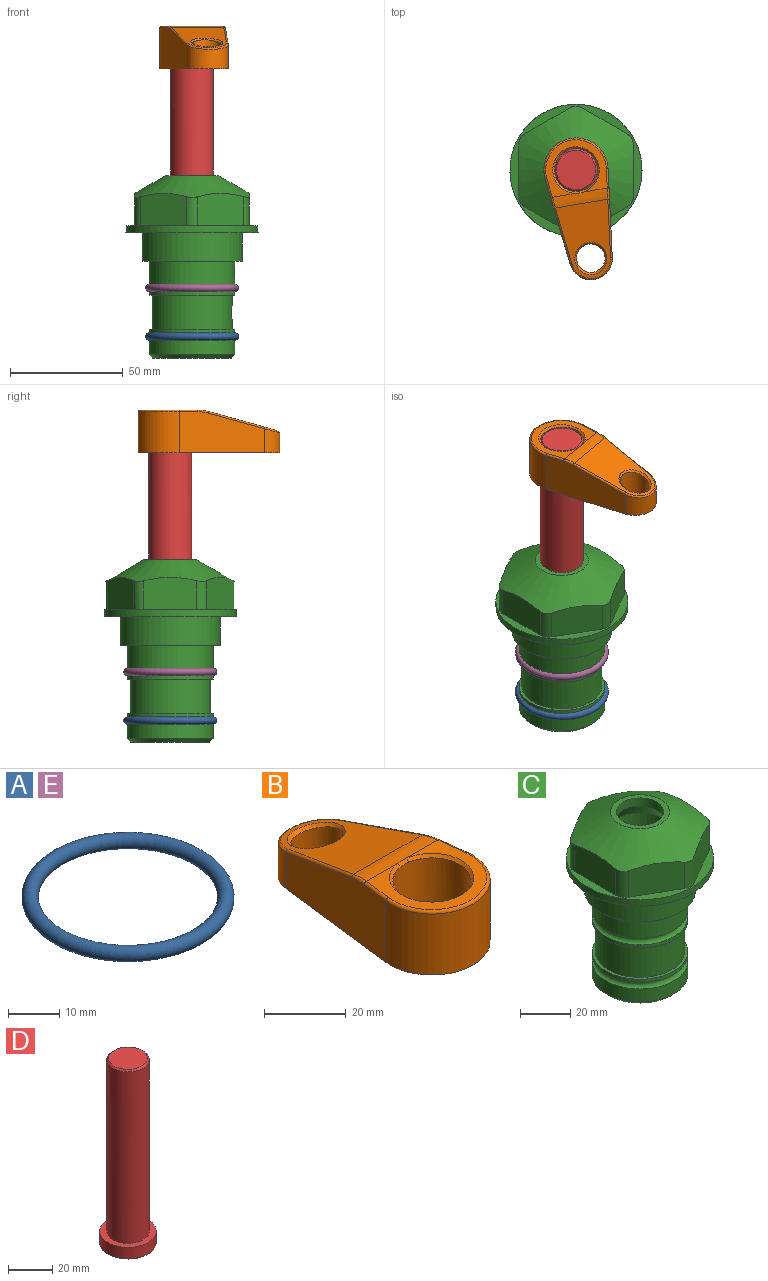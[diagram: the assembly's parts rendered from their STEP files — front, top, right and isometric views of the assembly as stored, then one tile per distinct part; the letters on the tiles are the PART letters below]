
ASSEMBLY  parts=5 mates=4
PART A: 1 faces, bbox 44.7x44.7x3.2 mm
  f0: torus R=19.05mm, axis (0,0,1), area 1193.9mm2
PART B: 31 faces, bbox 31.7x65.5x19.8 mm
  f0: plane 39.12x18.26mm, normal (0.99,0.12,0), area 612.2mm2, adj f1,f4,f7,f11,f13,f15
  f1: cylinder r=9.53mm len=18.91mm, axis (0,0,-1), area 296.1mm2, adj f0,f2,f7,f17
  f2: plane 39.12x18.26mm, normal (-0.99,0.12,0), area 612.2mm2, adj f1,f4,f7,f12,f14,f16
  f3: cylinder r=6.35mm len=12.7mm, axis (0,0,-1), area 362.4mm2, adj f7,f18
  f4: cylinder r=14.29mm len=28.58mm, axis (0,0,-1), area 882.2mm2, adj f0,f2,f7,f10
  f5: cylinder r=9.53mm len=19.05mm, axis (0,0,-1), area 1092.6mm2, adj f7,f19,f20
  f6: plane 26.99x23.69mm, normal (0,0,1), area 216.2mm2, adj f9,f10,f11,f12,f19
  f7: plane 63.5x28.58mm, normal (0,0,-1), area 661.8mm2, adj f0,f1,f2,f3,f4,f5,f22,f23
  f8: plane 33.52x23.6mm, normal (0,0.26,0.97), area 486mm2, adj f9,f15,f16,f17,f18
  f9: cylinder r=19.05mm len=24.72mm, axis (1,0,0), area 120.4mm2, adj f6,f8,f13,f14,f20
  f10: torus R=13.49mm, axis (0,0,1), area 59mm2, adj f4,f6,f11,f12
  f11: cylinder r=0.79mm len=8.67mm, axis (0.12,-0.99,0), area 10.8mm2, adj f0,f6,f10,f13
  f12: cylinder r=0.79mm len=8.67mm, axis (0.12,0.99,0), area 10.8mm2, adj f2,f6,f10,f14
  f13: bspline ~4.95x1.42mm, area 6.1mm2, adj f0,f9,f11,f15
  f14: bspline ~4.95x1.42mm, area 6.1mm2, adj f2,f9,f12,f16
  f15: cylinder r=0.79mm len=25.95mm, axis (0.12,-0.96,0.26), area 32.9mm2, adj f0,f8,f13,f17
  f16: cylinder r=0.79mm len=25.95mm, axis (0.12,0.96,-0.26), area 32.9mm2, adj f2,f8,f14,f17
  f17: bspline ~18.91x8.38mm, area 30mm2, adj f1,f8,f15,f16
  f18: bspline ~14.29x14.29mm, area 48.3mm2, adj f3,f8
  f19: cone r=9.53mm half-angle=45deg, axis (0,0,1), area 66.5mm2, adj f5,f6,f20
  f20: bspline ~3.22x0.96mm, area 3.5mm2, adj f5,f9,f19
  f21: plane 2.75x2.72mm, normal (0,0,-1), area 2.9mm2, adj f23,f25,f28
  f22: plane 23.05x15.88mm, normal (-0.99,-0.12,0), area 323.6mm2, adj f7,f25,f26,f27,f28,f29
  f23: plane 23.05x15.88mm, normal (0.99,-0.12,0), area 323.6mm2, adj f7,f21,f25,f27,f28,f30
  f24: cylinder r=9.53mm len=10.69mm, axis (0,0,-1), area 114.7mm2, adj f7,f27,f29,f30
  f25: cylinder r=12.7mm len=20.59mm, axis (0,0,-1), area 381.1mm2, adj f7,f21,f22,f23,f26,f28
  f26: plane 2.75x2.72mm, normal (0,0,-1), area 2.9mm2, adj f22,f25,f28
  f27: plane 19.72x18.37mm, normal (0,-0.26,-0.97), area 291.8mm2, adj f22,f23,f24,f28,f29,f30
  f28: cylinder r=15.88mm len=19.92mm, axis (1,0,0), area 54.8mm2, adj f21,f22,f23,f25,f26,f27
  f29: cylinder r=1.59mm len=11mm, axis (0,0,-1), area 34.7mm2, adj f7,f22,f24,f27
  f30: cylinder r=1.59mm len=11mm, axis (0,0,-1), area 34.7mm2, adj f7,f23,f24,f27
PART C: 36 faces, bbox 58.7x58.7x81 mm
  f0: cylinder r=17.78mm len=35.56mm, axis (0,0,1), area 1670.8mm2, adj f23,f24,f31
  f1: cylinder r=19.05mm len=38.1mm, axis (0,0,1), area 1191.9mm2, adj f26,f27,f30
  f2: plane 58.66x58.66mm, normal (0,0,-1), area 1150.6mm2, adj f3,f28
  f3: cylinder r=29.33mm len=58.66mm, axis (0,0,-1), area 585.1mm2, adj f2,f4
  f4: plane 58.66x58.66mm, normal (0,0,1), area 475.9mm2, adj f3,f5,f6,f7,f8,f9,f10,f11
  f5: plane 20.32x14.34mm, normal (-0.5,0.87,0), area 324.4mm2, adj f4,f15,f16,f17
  f6: plane 20.32x14.34mm, normal (0.5,0.87,0), area 324.4mm2, adj f4,f14,f15,f17
  f7: plane 23.48x14.34mm, normal (1,0,0), area 324.4mm2, adj f4,f13,f14,f17
  f8: plane 20.32x14.34mm, normal (0.5,-0.87,0), area 324.4mm2, adj f4,f12,f13,f17
  f9: plane 20.32x14.34mm, normal (-0.5,-0.87,0), area 324.4mm2, adj f4,f11,f12,f17
  f10: plane 23.48x14.34mm, normal (-1,0,0), area 324.4mm2, adj f4,f11,f16,f17
  f11: cylinder r=5.08mm len=12.85mm, axis (0,0,-1), area 67.2mm2, adj f4,f9,f10,f17
  f12: cylinder r=5.08mm len=12.85mm, axis (0,0,-1), area 67.2mm2, adj f4,f8,f9,f17
  f13: cylinder r=5.08mm len=12.85mm, axis (0,0,-1), area 67.2mm2, adj f4,f7,f8,f17
  f14: cylinder r=5.08mm len=12.85mm, axis (0,0,-1), area 67.2mm2, adj f4,f6,f7,f17
  f15: cylinder r=5.08mm len=12.85mm, axis (0,0,-1), area 67.2mm2, adj f4,f5,f6,f17
  f16: cylinder r=5.08mm len=12.85mm, axis (0,0,-1), area 67.2mm2, adj f4,f5,f10,f17
  f17: cone r=11.73mm half-angle=60deg, axis (0,0,-1), area 2071.8mm2, adj f5,f6,f7,f8,f9,f10,f11,f12
  f18: plane 23.46x23.46mm, normal (0,0,1), area 147.4mm2, adj f17,f35
  f19: plane 34.93x34.93mm, normal (0,0,-1), area 958mm2, adj f29
  f20: cylinder r=19.05mm len=38.1mm, axis (0,0,1), area 760.1mm2, adj f21,f29
  f21: torus R=19.05mm, axis (0,0,1), area 565.3mm2, adj f20,f22
  f22: cylinder r=19.05mm len=38.1mm, axis (0,0,1), area 190mm2, adj f21,f23
  f23: plane 38.1x38.1mm, normal (0,0,1), area 146.9mm2, adj f0,f22
  f24: plane 38.1x38.1mm, normal (0,0,-1), area 146.9mm2, adj f0,f25
  f25: cylinder r=19.05mm len=38.1mm, axis (0,0,1), area 190mm2, adj f24,f26
  f26: torus R=19.05mm, axis (0,0,1), area 565.3mm2, adj f1,f25
  f27: plane 44.45x44.45mm, normal (0,0,-1), area 411.7mm2, adj f1,f28
  f28: cylinder r=22.23mm len=44.45mm, axis (0,0,1), area 1773.5mm2, adj f2,f27
  f29: cone r=19.05mm half-angle=45deg, axis (0,0,1), area 257.5mm2, adj f19,f20
  f30: cylinder r=3.17mm len=6.75mm, axis (-1,0,0), area 128mm2, adj f1,f33
  f31: cylinder r=3.17mm len=6.35mm, axis (-1,0,0), area 102.5mm2, adj f0,f33
  f32: plane 25.4x25.4mm, normal (0,0,1), area 506.7mm2, adj f33
  f33: cylinder r=12.7mm len=66.42mm, axis (0,0,-1), area 5236.2mm2, adj f30,f31,f32,f34
  f34: cone r=9.53mm half-angle=30deg, axis (0,0,-1), area 443.4mm2, adj f33,f35
  f35: cylinder r=9.53mm len=19.05mm, axis (0,0,-1), area 240.9mm2, adj f18,f34
PART D: 6 faces, bbox 25.4x25.4x101.6 mm
  f0: plane 17.46x17.46mm, normal (0,0,1), area 239.5mm2, adj f5
  f1: plane 25.4x25.4mm, normal (0,0,-1), area 506.7mm2, adj f2
  f2: cylinder r=12.7mm len=25.4mm, axis (0,0,1), area 506.7mm2, adj f1,f3
  f3: plane 25.4x25.4mm, normal (0,0,1), area 221.7mm2, adj f2,f4
  f4: cylinder r=9.53mm len=94.46mm, axis (0,0,1), area 5653mm2, adj f3,f5
  f5: cone r=8.73mm half-angle=45deg, axis (0,0,-1), area 64.4mm2, adj f0,f4
PART E: same geometry as A
PLACE A t=(0,0,-21.59)mm
PLACE B rot(axis=(0,0,-1),170.4deg) t=(0,0,28.35)mm
PLACE C at identity fixed
PLACE D rot(axis=(0,0,-1),170.4deg) t=(0,0,27.55)mm
PLACE E at identity
MATE fastened B.f4 <-> D.f2  axis (0,0,-1) through (0,0,91.05)mm
MATE fastened E.f0 <-> C.f0  axis (0,0,1) through (0,0,-24.51)mm
MATE cylindrical D.f2 <-> C.f0  axis (0,0,-1) through (0,0,-10.55)mm
MATE fastened A.f0 <-> C.f0  axis (0,0,1) through (0,0,-46.1)mm
